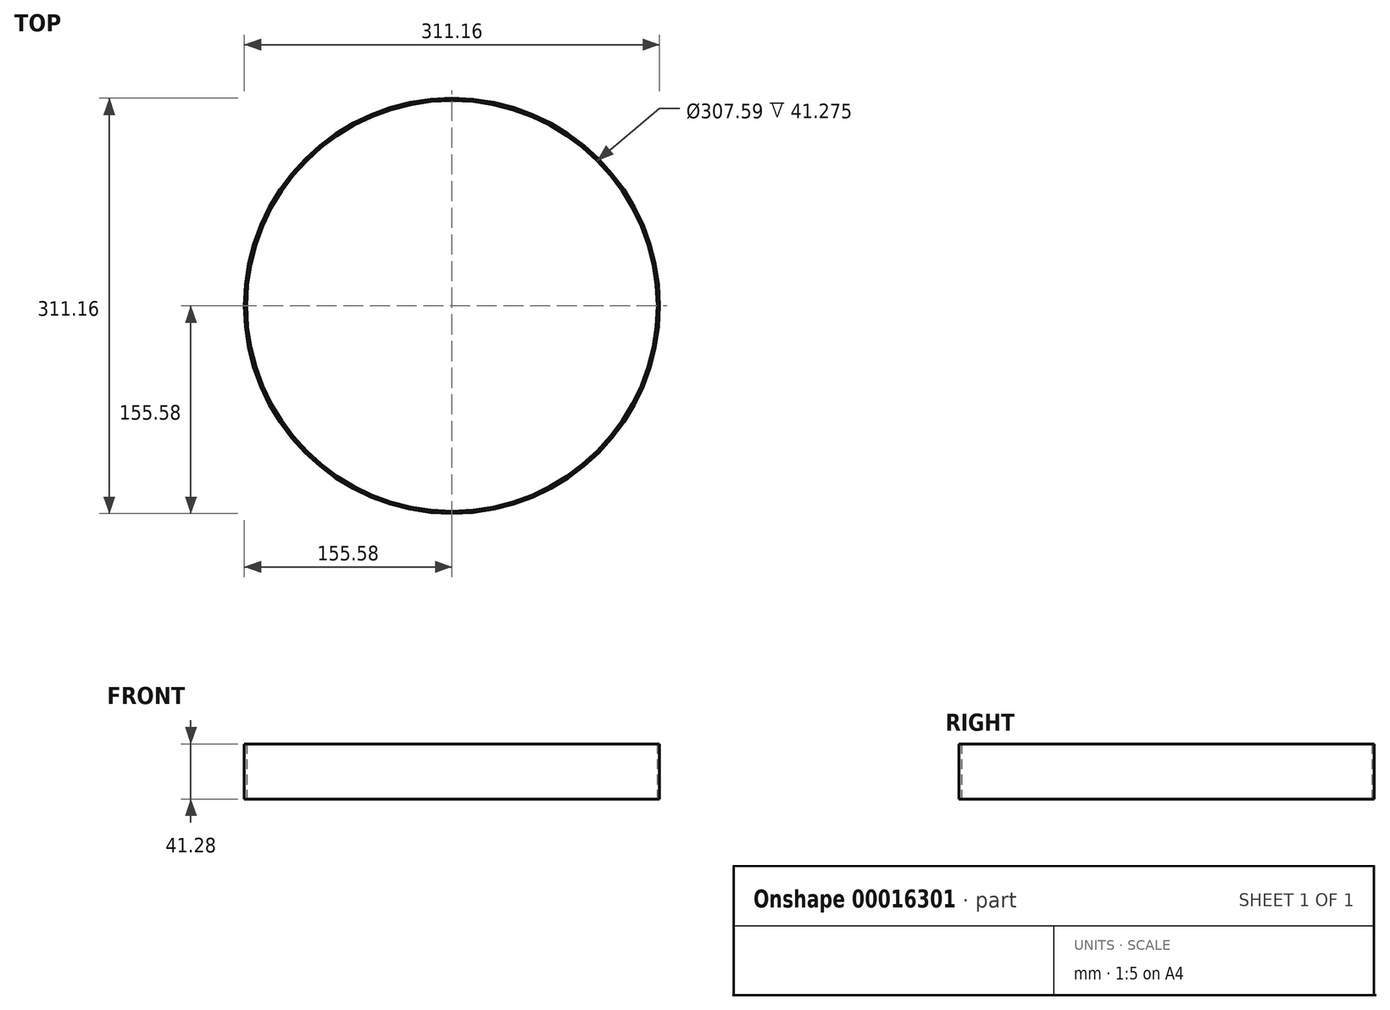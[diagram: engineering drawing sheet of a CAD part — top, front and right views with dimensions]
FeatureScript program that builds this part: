
annotation { "Feature Type Name" : "Feature", "Feature Type Description" : "" }
export const myFeature = defineFeature(function(context is Context, id is Id, definition is map)
    precondition{}
    {
        {
            var Q0;
            Q0=qCreatedBy(makeId("Top.planeOp"),FACE);
            var sketch = newSketch(context, id + "F0", { "sketchPlane" : qUnion([Q0])});
            skCircle(sketch, "E0", {"center": v(0, 0) * mm, "radius": 155.58 * mm});
            skCircle(sketch, "E1", {"center": v(0, 0) * mm, "radius": 153.8 * mm});
            skSolve(sketch);
        }
        {
            var Q0;
            Q0 = qSketchRegion(id + "F0", true);
            extrude(context, id + "F1", {"entities" : qUnion([Q0]), "depth" : 41.27 * mm});
        }
    });
